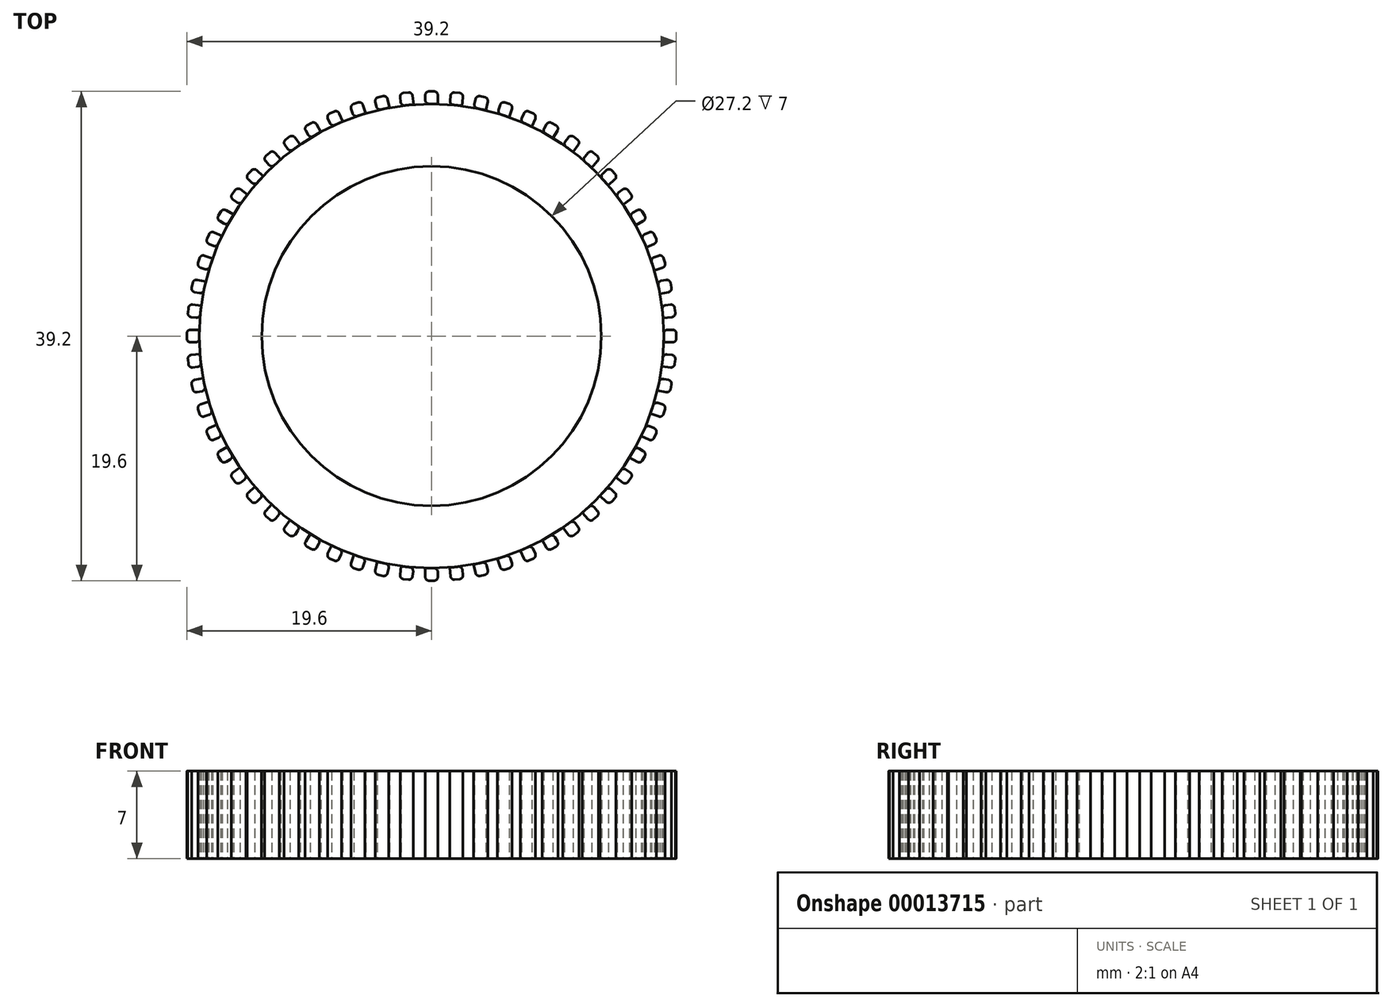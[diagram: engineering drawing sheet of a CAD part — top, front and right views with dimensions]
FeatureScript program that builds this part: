
annotation { "Feature Type Name" : "Feature", "Feature Type Description" : "" }
export const myFeature = defineFeature(function(context is Context, id is Id, definition is map)
    precondition{}
    {
        {
            var Q0;
            Q0=qCreatedBy(makeId("Top.planeOp"),FACE);
            var sketch = newSketch(context, id + "F0", { "sketchPlane" : qUnion([Q0])});
            skCircle(sketch, "E0", {"center": v(0, 0) * mm, "radius": 18.6 * mm});
            skLineSegment(sketch, "E1", {"start": v(0, 0) * mm, "end": v(0, 18.6) * mm, "construction": true});
            skLineSegment(sketch, "E2", {"start": v(-0.5, 18.6) * mm, "end": v(-0.5, 19.6) * mm});
            skLineSegment(sketch, "E3", {"start": v(0.5, 18.6) * mm, "end": v(0.5, 19.6) * mm});
            skLineSegment(sketch, "E4", {"start": v(0.5, 19.6) * mm, "end": v(0, 19.6) * mm});
            skLineSegment(sketch, "E5", {"start": v(-0.5, 19.6) * mm, "end": v(0, 19.6) * mm});
            skCircle(sketch, "E6", {"center": v(0, 0) * mm, "radius": 13.6 * mm});
            skCircle(sketch, "E7", {"center": v(0, 0) * mm, "radius": 4 * mm});
            skCircle(sketch, "E8", {"center": v(0, 0) * mm, "radius": 6 * mm});
            skLineSegment(sketch, "E9", {"start": v(2, 13.45) * mm, "end": v(2, 5.66) * mm});
            skLineSegment(sketch, "E10", {"start": v(-2, 13.45) * mm, "end": v(-2, 5.66) * mm});
            skLineSegment(sketch, "E11", {"start": v(-13.45, 2) * mm, "end": v(-5.66, 2) * mm});
            skLineSegment(sketch, "E12", {"start": v(13.45, -2) * mm, "end": v(5.66, -2) * mm});
            skLineSegment(sketch, "E13.trimOffspring", {"start": v(2, -5.66) * mm, "end": v(2, -13.45) * mm});
            skLineSegment(sketch, "E14.trimOffspring", {"start": v(-2, -5.66) * mm, "end": v(-2, -13.45) * mm});
            skLineSegment(sketch, "E15.trimOffspring", {"start": v(5.66, 2) * mm, "end": v(13.45, 2) * mm});
            skLineSegment(sketch, "E16.trimOffspring", {"start": v(-5.66, -2) * mm, "end": v(-13.45, -2) * mm});
            skSolve(sketch);
        }
        {
            var Q0;
            {var subQ0=sQuery(id+"F0.wireOp",EDGE,"E1");Q0=makeQuery(id+"F0.imprint","IMPRINT",FACE,{"disambiguationData":[TD([[makeQuery(id+"F0.imprint","IMPRINT",EDGE,{"derivedFrom":subQ0}),1.0]])]});}
            var Q1;
            {var subQ9=sQuery(id+"F0.wireOp",EDGE,"E0");var subQ11=makeQuery(id+"F0.imprint","INTERSECT",VERTEX,{"derivedFrom":[subQ9,sQuery(id+"F0.wireOp",EDGE,"E2")]});Q1=makeQuery(id+"F0.imprint","IMPRINT",FACE,{"disambiguationData":[TD([[makeQuery(id+"F0.imprint","IMPRINT",EDGE,{"disambiguationData":[TD([[subQ11,1.0]])],"derivedFrom":subQ9}),1.0]])]});}
            extrude(context, id + "F1", {"entities" : qUnion([Q0, Q1]), "depth" : 7 * mm});
        }
        {
            var Q0;
            {var subQ1=sQuery(id+"F0.wireOp",EDGE,"E2");Q0=makeQuery(id+"F0.imprint","IMPRINT",FACE,{"disambiguationData":[TD([[makeQuery(id+"F0.imprint","IMPRINT",EDGE,{"derivedFrom":subQ1}),-1.0]])]});}
            extrude(context, id + "F2", {"entities" : qUnion([Q0]), "depth" : 7 * mm});
        }
        {
            var Q0;
            Q0=makeQuery(id+"F2.opExtrude","SWEPT_EDGE",EDGE,{"disambiguationData":[OSD([sQuery(id+"F0.wireOp",EDGE,"E3"),sQuery(id+"F0.wireOp",EDGE,"E4")])]});
            var Q1;
            Q1=makeQuery(id+"F2.opExtrude","SWEPT_EDGE",EDGE,{"disambiguationData":[OSD([sQuery(id+"F0.wireOp",EDGE,"E2"),sQuery(id+"F0.wireOp",EDGE,"E4")])]});
            fillet(context, id + "F3", {"entities" : qUnion([Q0, Q1]), "radius" : 0.3 * mm, "tangentPropagation" : true, "allowEdgeOverflow" : false});
        }
        {
            var Q0;
            Q0=makeQuery(id+"F2.opExtrude","SWEPT_BODY",BODY,{"disambiguationData":[OSD([sQuery(id+"F0.wireOp",EDGE,"E0"),sQuery(id+"F0.wireOp",EDGE,"E2"),sQuery(id+"F0.wireOp",EDGE,"E3"),sQuery(id+"F0.wireOp",EDGE,"E4")])]});
            var Q1;
            Q1=sQuery(id+"F0.wireOp",EDGE,"E0");
            circularPattern(context, id + "F4", {"entities" : qUnion([Q0]), "axis" : qUnion([Q1]), "angle" : 360 * degree, "instanceCount" : round(60), "equalSpace" : true});
        }
    });
